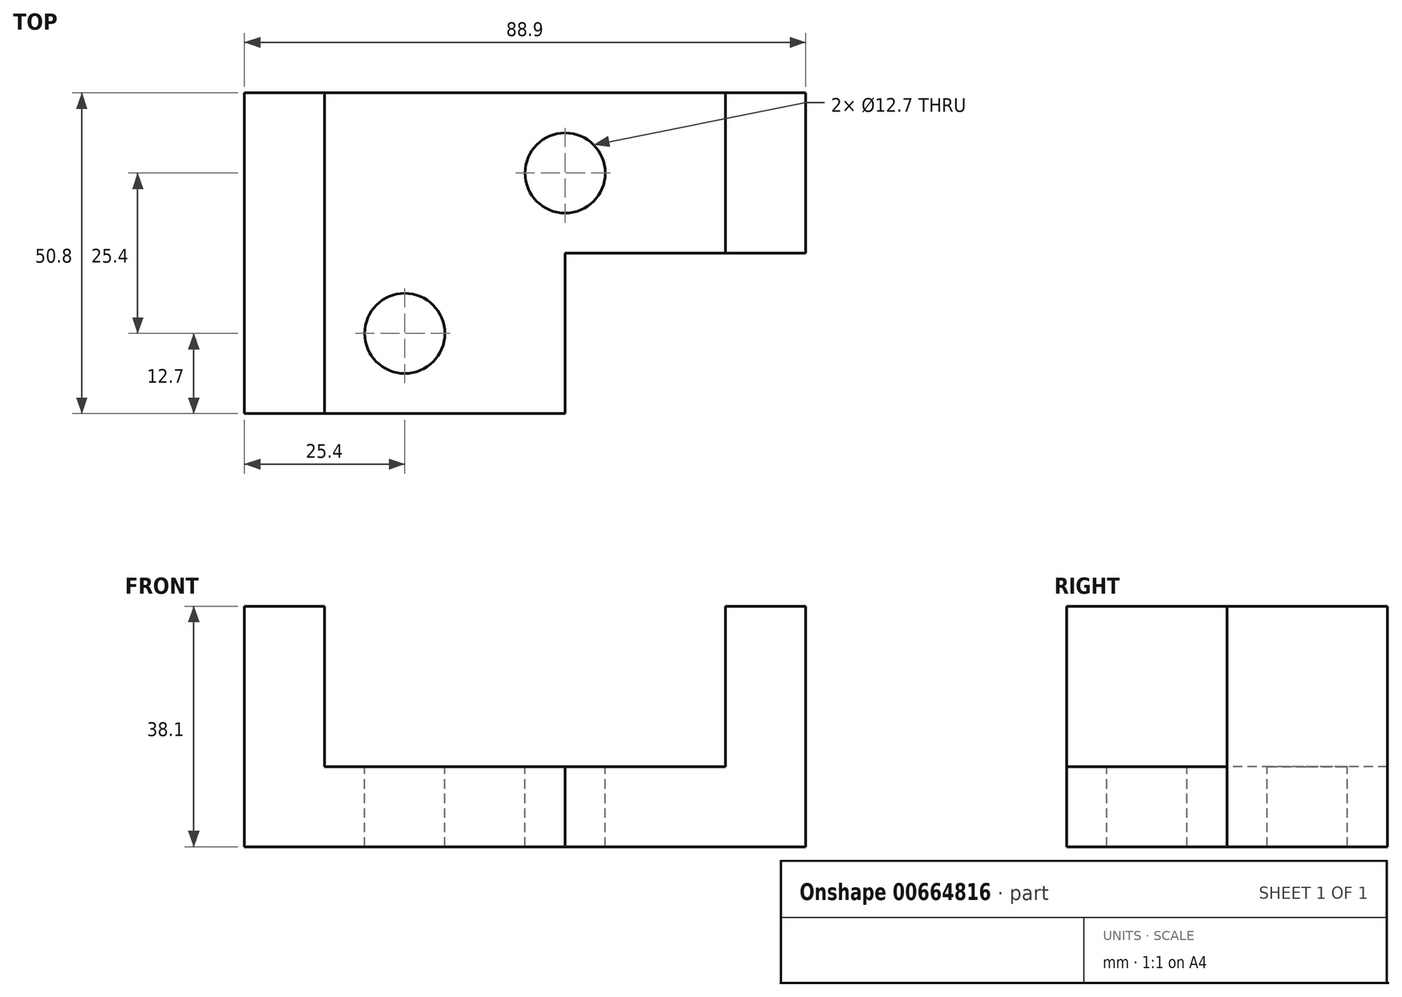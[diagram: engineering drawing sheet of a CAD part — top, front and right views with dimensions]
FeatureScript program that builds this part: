
annotation { "Feature Type Name" : "Feature", "Feature Type Description" : "" }
export const myFeature = defineFeature(function(context is Context, id is Id, definition is map)
    precondition{}
    {
        {
            var Q0;
            Q0=qCreatedBy(makeId("Front.planeOp"),FACE);
            var sketch = newSketch(context, id + "F0", { "sketchPlane" : qUnion([Q0])});
            skLineSegment(sketch, "E0.bottom", {"start": v(-40.84, 29.23) * mm, "end": v(48.06, 29.23) * mm});
            skLineSegment(sketch, "E0.top", {"start": v(-40.84, -8.87) * mm, "end": v(48.06, -8.87) * mm});
            skLineSegment(sketch, "E0.left", {"start": v(-40.84, 29.23) * mm, "end": v(-40.84, -8.87) * mm});
            skLineSegment(sketch, "E0.right", {"start": v(48.06, 29.23) * mm, "end": v(48.06, -8.87) * mm});
            skSolve(sketch);
        }
        {
            var Q0;
            Q0 = qSketchRegion(id + "F0", true);
            extrude(context, id + "F1", {"entities" : qUnion([Q0]), "depth" : 50.8 * mm, "offsetDistance" : 25.4 * mm});
        }
        {
            var Q0;
            Q0=makeQuery(id+"F1.opExtrude","CAP_FACE",FACE,{"disambiguationData":[OSD([sQuery(id+"F0.wireOp",EDGE,"E0.bottom"),sQuery(id+"F0.wireOp",EDGE,"E0.top"),sQuery(id+"F0.wireOp",EDGE,"E0.left"),sQuery(id+"F0.wireOp",EDGE,"E0.right")])],"isStart":false});
            var sketch = newSketch(context, id + "F2", { "sketchPlane" : qUnion([Q0])});
            skLineSegment(sketch, "E1.bottom", {"start": v(-28.14, 29.23) * mm, "end": v(35.36, 29.23) * mm});
            skLineSegment(sketch, "E1.top", {"start": v(-28.14, 3.83) * mm, "end": v(35.36, 3.83) * mm});
            skLineSegment(sketch, "E1.left", {"start": v(-28.14, 29.23) * mm, "end": v(-28.14, 3.83) * mm});
            skLineSegment(sketch, "E1.right", {"start": v(35.36, 29.23) * mm, "end": v(35.36, 3.83) * mm});
            skSolve(sketch);
        }
        {
            var Q0;
            Q0=makeQuery(id+"F2.imprint","IMPRINT",FACE,{"disambiguationData":[TD([[makeQuery(id+"F2.imprint","IMPRINT",EDGE,{"derivedFrom":sQuery(id+"F2.wireOp",EDGE,"E1.bottom")}),-1.0]])]});
            extrude(context, id + "F3", {"entities" : qUnion([Q0]), "operationType" : NewBodyOperationType.REMOVE, "oppositeDirection" : true, "depth" : 25.4 * mm, "offsetDistance" : 25.4 * mm});
        }
        {
            var Q0;
            Q0=makeQuery(id+"F3.boolean.opBoolean","COPY",FACE,{"derivedFrom":makeQuery(id+"F3.opExtrude","CAP_FACE",FACE,{"disambiguationData":[OSD([sQuery(id+"F2.wireOp",EDGE,"E1.bottom"),sQuery(id+"F2.wireOp",EDGE,"E1.top"),sQuery(id+"F2.wireOp",EDGE,"E1.left"),sQuery(id+"F2.wireOp",EDGE,"E1.right")])],"isStart":false})});
            extrude(context, id + "F4", {"entities" : qUnion([Q0]), "operationType" : NewBodyOperationType.REMOVE, "oppositeDirection" : true, "depth" : 25.4 * mm, "offsetDistance" : 25.4 * mm});
        }
        {
            var Q0;
            Q0=makeQuery(id+"F1.opExtrude","SWEPT_FACE",FACE,{"disambiguationData":[OSD([sQuery(id+"F0.wireOp",EDGE,"E0.right")])]});
            var sketch = newSketch(context, id + "F5", { "sketchPlane" : qUnion([Q0])});
            skLineSegment(sketch, "E2.bottom", {"start": v(-50.8, 29.23) * mm, "end": v(-25.4, 29.23) * mm});
            skLineSegment(sketch, "E2.top", {"start": v(-50.8, -8.87) * mm, "end": v(-25.4, -8.87) * mm});
            skLineSegment(sketch, "E2.left", {"start": v(-50.8, 29.23) * mm, "end": v(-50.8, -8.87) * mm});
            skLineSegment(sketch, "E2.right", {"start": v(-25.4, 29.23) * mm, "end": v(-25.4, -8.87) * mm});
            skSolve(sketch);
        }
        {
            var Q0;
            Q0 = qSketchRegion(id + "F5", true);
            extrude(context, id + "F6", {"entities" : qUnion([Q0]), "operationType" : NewBodyOperationType.REMOVE, "oppositeDirection" : true, "depth" : 38.1 * mm, "offsetDistance" : 25.4 * mm});
        }
        {
            var Q0;
            {var subQ0=sQuery(id+"F2.wireOp",EDGE,"E1.top");Q0=makeQuery(id+"F4.boolean.opBoolean","MERGE",FACE,{"derivedFrom":[makeQuery(id+"F3.boolean.opBoolean","COPY",FACE,{"derivedFrom":makeQuery(id+"F3.opExtrude","SWEPT_FACE",FACE,{"disambiguationData":[OSD([subQ0])]})}),makeQuery(id+"F4.opExtrude","SWEPT_FACE",FACE,{"disambiguationData":[OSD([subQ0])]})]});}
            var sketch = newSketch(context, id + "F7", { "sketchPlane" : qUnion([Q0])});
            skCircle(sketch, "E3", {"center": v(-15.44, -38.1) * mm, "radius": 6.35 * mm});
            skSolve(sketch);
        }
        {
            var Q0;
            Q0 = qSketchRegion(id + "F7", true);
            extrude(context, id + "F8", {"entities" : qUnion([Q0]), "operationType" : NewBodyOperationType.REMOVE, "endBound" : BoundingType.THROUGH_ALL, "oppositeDirection" : true, "depth" : 25.4 * mm, "offsetDistance" : 25.4 * mm});
        }
        {
            var Q0;
            {var subQ0=sQuery(id+"F2.wireOp",EDGE,"E1.top");Q0=makeQuery(id+"F4.boolean.opBoolean","MERGE",FACE,{"derivedFrom":[makeQuery(id+"F3.boolean.opBoolean","COPY",FACE,{"derivedFrom":makeQuery(id+"F3.opExtrude","SWEPT_FACE",FACE,{"disambiguationData":[OSD([subQ0])]})}),makeQuery(id+"F4.opExtrude","SWEPT_FACE",FACE,{"disambiguationData":[OSD([subQ0])]})]});}
            var sketch = newSketch(context, id + "F9", { "sketchPlane" : qUnion([Q0])});
            skCircle(sketch, "E4", {"center": v(9.96, -12.7) * mm, "radius": 6.35 * mm});
            skSolve(sketch);
        }
        {
            var Q0;
            Q0 = qSketchRegion(id + "F9", true);
            extrude(context, id + "F10", {"entities" : qUnion([Q0]), "operationType" : NewBodyOperationType.REMOVE, "endBound" : BoundingType.THROUGH_ALL, "oppositeDirection" : true, "depth" : 25.4 * mm, "offsetDistance" : 25.4 * mm});
        }
    });
